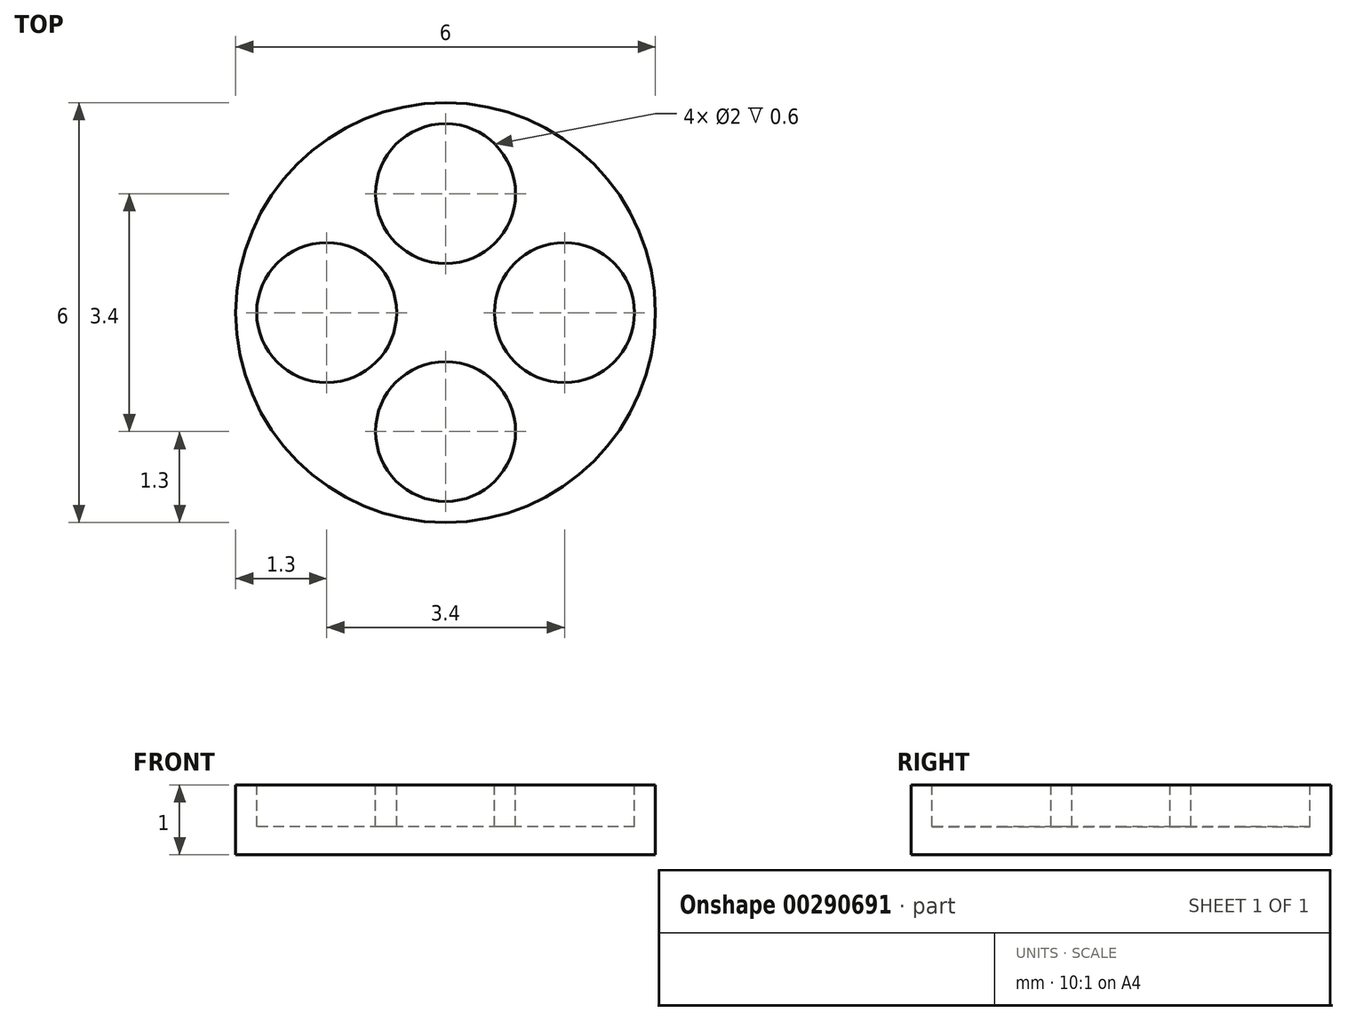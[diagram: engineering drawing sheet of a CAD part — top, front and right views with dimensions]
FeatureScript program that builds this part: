
annotation { "Feature Type Name" : "Feature", "Feature Type Description" : "" }
export const myFeature = defineFeature(function(context is Context, id is Id, definition is map)
    precondition{}
    {
        {
            var Q0;
            Q0=qCreatedBy(makeId("Top.planeOp"),FACE);
            var sketch = newSketch(context, id + "F0", { "sketchPlane" : qUnion([Q0])});
            skCircle(sketch, "E0", {"center": v(0, 0) * mm, "radius": 3 * mm});
            skSolve(sketch);
        }
        {
            var Q0;
            Q0 = qSketchRegion(id + "F0", true);
            extrude(context, id + "F1", {"entities" : qUnion([Q0]), "depth" : 1 * mm});
        }
        {
            var Q0;
            Q0=makeQuery(id+"F1.opExtrude","CAP_FACE",FACE,{"disambiguationData":[OSD([sQuery(id+"F0.wireOp",EDGE,"E0")])],"isStart":false});
            var sketch = newSketch(context, id + "F2", { "sketchPlane" : qUnion([Q0])});
            skLineSegment(sketch, "E1", {"start": v(0, 0) * mm, "end": v(0, 1.7) * mm, "construction": true});
            skCircle(sketch, "E2", {"center": v(0, 1.7) * mm, "radius": 1 * mm});
            skCircle(sketch, "E3.1.0", {"center": v(-1.7, 0) * mm, "radius": 1 * mm});
            skCircle(sketch, "E3.2.0", {"center": v(0, -1.7) * mm, "radius": 1 * mm});
            skCircle(sketch, "E3.3.0", {"center": v(1.7, 0) * mm, "radius": 1 * mm});
            skPoint(sketch, "E3.center", {"position": v(0, 0) * mm});
            skSolve(sketch);
        }
        {
            var Q0;
            Q0 = qSketchRegion(id + "F2", true);
            extrude(context, id + "F3", {"entities" : qUnion([Q0]), "operationType" : NewBodyOperationType.REMOVE, "oppositeDirection" : true, "depth" : 0.6 * mm});
        }
    });
